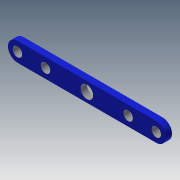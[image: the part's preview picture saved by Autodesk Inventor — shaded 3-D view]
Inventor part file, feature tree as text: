
AUTODESK INVENTOR PART (.ipt)
format: ipt  version: 2013 (Build 170138000, 138)  size: 156,672 bytes
history: native  units: mm
features: sketch x12, extrude x11
ambient origin geometry x8: Origin, YZ Plane, XZ Plane, XY Plane, X Axis, Y Axis, Z Axis, Center Point
bodies: Solid1 (feature_tree)
feature tree (23):
  extrude  "Extrusion1"  Depth=6.0mm
  extrude  "Extrusion2"  Depth=6.0mm
  extrude  "Extrusion3"  Depth=3.0mm
  extrude  "Extrusion4"  Depth=3.0mm
  extrude  "Extrusion5"  Depth=10.0mm
  extrude  "Extrusion6"  Depth=2.0mm TaperAngle=0.0deg
  extrude  "Extrusion7"  Depth=0.2mm
  extrude  "Extrusion8"  Depth=0.2mm
  extrude  "Extrusion9"  Depth=0.2mm
  extrude  "Extrusion10"  Depth=12.985mm
  sketch  "Sketch11"  dims[d25=0.2mm d26=12.985mm]
  sketch  "Sketch12"  dims[d27=0.2mm d28=2.0mm d29=0.0mm d30=2.0mm d31=0.0mm d32=2.0mm d33=0.0mm d35=0.2mm d36=0.2mm d37=2.0mm d38=0.0mm d44=2.0mm d45=0.0mm d46=2.0mm d47=0.0mm]
  extrude  "Extrusion11"  Depth=12.985mm
  sketch  "Sketch1"  dims[d0=44.0mm d1=6.0mm]
  sketch  "Sketch2"  dims[d2=6.0mm d3=6.0mm]
  sketch  "Sketch3"  dims[d4=2.0mm d5=0.0mm d6=3.0mm]
  sketch  "Sketch4"  dims[d7=3.0mm d8=3.0mm]
  sketch  "Sketch5"  dims[d9=2.0mm d10=0.0mm d11=10.0mm]
  sketch  "Sketch6"  dims[d12=3.0mm d13=2.0mm d14=0.0mm]
  sketch  "Sketch7"  dims[d15=0.2mm d16=0.2mm]
  sketch  "Sketch8"  dims[d17=0.2mm d18=0.2mm]
  sketch  "Sketch9"  dims[d19=2.0mm d20=0.0mm d21=0.2mm]
  sketch  "Sketch10"  dims[d22=2.0mm d23=0.0mm d24=12.985mm]
